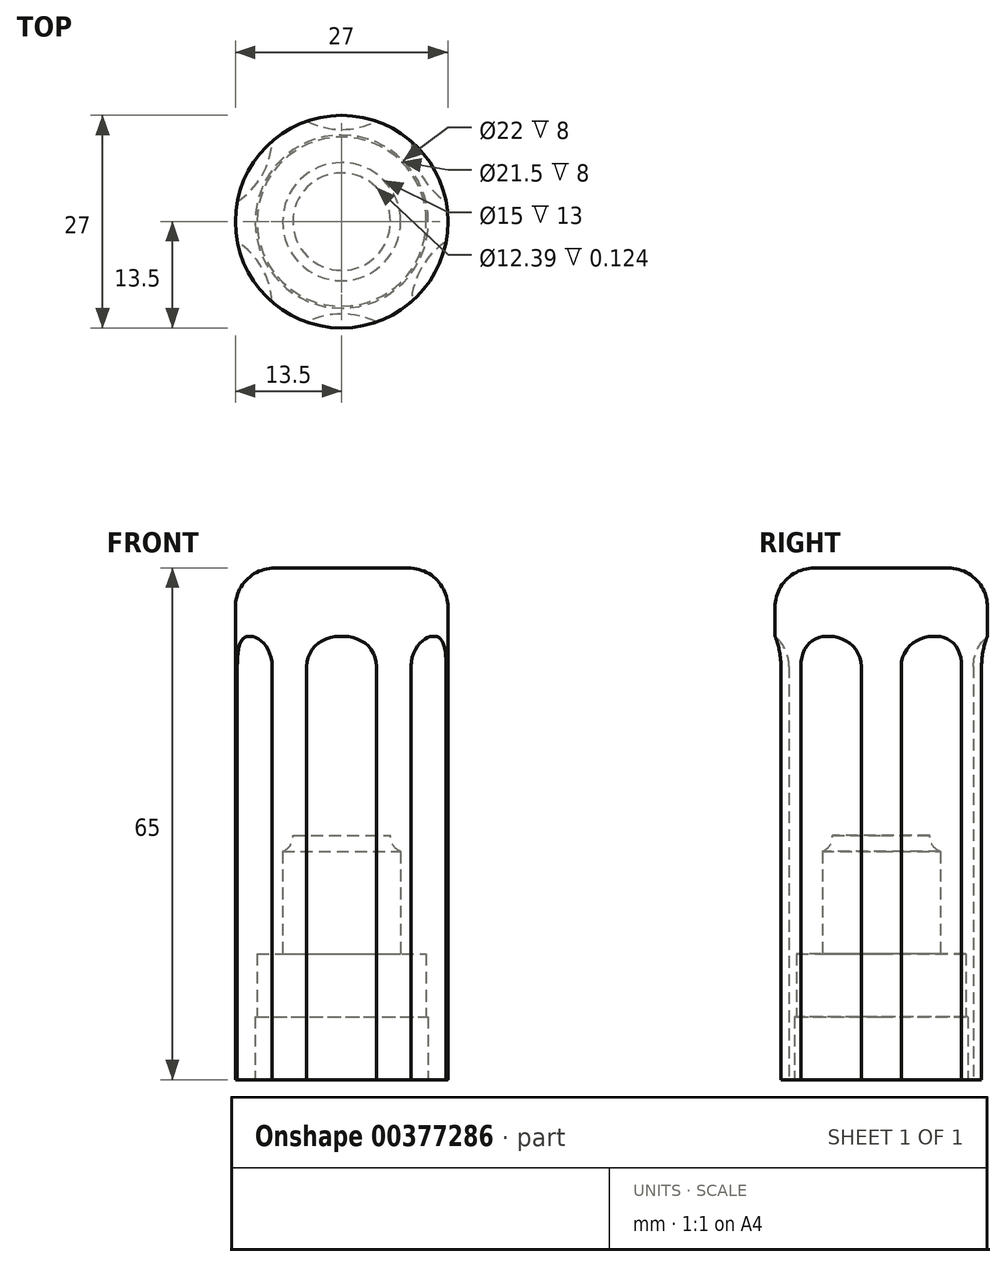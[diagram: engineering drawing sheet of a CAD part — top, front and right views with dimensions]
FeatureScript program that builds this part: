
annotation { "Feature Type Name" : "Feature", "Feature Type Description" : "" }
export const myFeature = defineFeature(function(context is Context, id is Id, definition is map)
    precondition{}
    {
        {
            var Q0;
            Q0=qCreatedBy(makeId("Front.planeOp"),FACE);
            var sketch = newSketch(context, id + "F0", { "sketchPlane" : qUnion([Q0])});
            skLineSegment(sketch, "E0", {"start": v(0, 32.45) * mm, "end": v(0, -32.55) * mm});
            skPoint(sketch, "E1.end.orphan", {"position": v(18.69, -28.88) * mm});
            skPoint(sketch, "E2.end.orphan", {"position": v(18.69, -32.55) * mm});
            skLineSegment(sketch, "E3", {"start": v(0, -32.55) * mm, "end": v(13.5, -32.55) * mm});
            skLineSegment(sketch, "E4", {"start": v(13.5, -32.55) * mm, "end": v(13.5, 27.45) * mm});
            skLineSegment(sketch, "E5", {"start": v(8.5, 32.45) * mm, "end": v(0, 32.45) * mm});
            skPoint(sketch, "E6.visualSharp", {"position": v(13.5, 32.45) * mm});
            skArc(sketch, "E6.filletArc", {"start": v(13.5, 27.45) * mm, "mid": v(12.04, 30.99) * mm, "end": v(8.5, 32.45) * mm});
            skSolve(sketch);
        }
        {
            var Q0;
            Q0=qSketchRegion(id+"F0",true);
            var Q1;
            Q1=sQuery(id+"F0.wireOp",EDGE,"E0");
            revolve(context, id + "F1", {"entities" : qUnion([Q0]), "axis" : qUnion([Q1]), "revolveType" : RevolveType.FULL});
        }
        {
            var Q0;
            Q0=makeQuery(id+"F1.opRevolve","SWEPT_FACE",FACE,{"disambiguationData":[OSD([sQuery(id+"F0.wireOp",EDGE,"E3")])]});
            var sketch = newSketch(context, id + "F2", { "sketchPlane" : qUnion([Q0])});
            skCircle(sketch, "E7.cCircle", {"center": v(0, 0) * mm, "radius": 13.5 * mm, "construction": true});
            skLineSegment(sketch, "E7.0", {"start": v(-13.5, -7.8) * mm, "end": v(-13.5, 7.8) * mm});
            skLineSegment(sketch, "E7.1", {"start": v(-13.5, 7.8) * mm, "end": v(0, 15.59) * mm});
            skLineSegment(sketch, "E7.2", {"start": v(0, 15.59) * mm, "end": v(13.5, 7.8) * mm});
            skLineSegment(sketch, "E7.3", {"start": v(13.5, 7.8) * mm, "end": v(13.5, -7.8) * mm});
            skLineSegment(sketch, "E7.4", {"start": v(13.5, -7.8) * mm, "end": v(0, -15.59) * mm});
            skLineSegment(sketch, "E7.5", {"start": v(0, -15.59) * mm, "end": v(-13.5, -7.8) * mm});
            skPoint(sketch, "E7.0.midPoint", {"position": v(-13.5, 0) * mm});
            skLineSegment(sketch, "E8.0", {"start": v(-13.5, -4.91) * mm, "end": v(-13.5, 4.91) * mm});
            skLineSegment(sketch, "E8.1", {"start": v(-13.5, 4.91) * mm, "end": v(-7.18, 12.44) * mm});
            skLineSegment(sketch, "E8.2", {"start": v(-7.18, 12.44) * mm, "end": v(2.5, 14.15) * mm});
            skLineSegment(sketch, "E8.3", {"start": v(2.5, 14.15) * mm, "end": v(11, 9.23) * mm});
            skLineSegment(sketch, "E8.4", {"start": v(11, 9.23) * mm, "end": v(14.37, 0) * mm});
            skLineSegment(sketch, "E8.5", {"start": v(14.37, 0) * mm, "end": v(11, -9.23) * mm});
            skLineSegment(sketch, "E8.6", {"start": v(11, -9.23) * mm, "end": v(2.5, -14.15) * mm});
            skLineSegment(sketch, "E8.7", {"start": v(2.5, -14.15) * mm, "end": v(-7.18, -12.44) * mm});
            skLineSegment(sketch, "E8.8", {"start": v(-7.18, -12.44) * mm, "end": v(-13.5, -4.91) * mm});
            skLineSegment(sketch, "E9.0", {"start": v(13.5, 4.91) * mm, "end": v(13.5, -4.91) * mm});
            skLineSegment(sketch, "E9.1", {"start": v(13.5, -4.91) * mm, "end": v(7.18, -12.44) * mm});
            skLineSegment(sketch, "E9.2", {"start": v(7.18, -12.44) * mm, "end": v(-2.5, -14.15) * mm});
            skLineSegment(sketch, "E9.3", {"start": v(-2.5, -14.15) * mm, "end": v(-11, -9.23) * mm});
            skLineSegment(sketch, "E9.4", {"start": v(-11, -9.23) * mm, "end": v(-14.37, 0) * mm});
            skLineSegment(sketch, "E9.5", {"start": v(-14.37, 0) * mm, "end": v(-11, 9.23) * mm});
            skLineSegment(sketch, "E9.6", {"start": v(-11, 9.23) * mm, "end": v(-2.5, 14.15) * mm});
            skLineSegment(sketch, "E9.7", {"start": v(-2.5, 14.15) * mm, "end": v(7.18, 12.44) * mm});
            skLineSegment(sketch, "E9.8", {"start": v(7.18, 12.44) * mm, "end": v(13.5, 4.91) * mm});
            skPoint(sketch, "E9.0.midPoint", {"position": v(13.5, 0) * mm});
            skArc(sketch, "E10", {"start": v(-4.69, 12.88) * mm, "mid": v(0, 11.71) * mm, "end": v(4.69, 12.88) * mm});
            skArc(sketch, "E11", {"start": v(4.69, -12.88) * mm, "mid": v(0, -11.71) * mm, "end": v(-4.69, -12.88) * mm});
            skArc(sketch, "E12", {"start": v(-13.5, 2.38) * mm, "mid": v(-10.14, 5.86) * mm, "end": v(-8.81, 10.5) * mm});
            skArc(sketch, "E13", {"start": v(-8.81, -10.5) * mm, "mid": v(-10.14, -5.86) * mm, "end": v(-13.5, -2.38) * mm});
            skArc(sketch, "E14", {"start": v(13.5, -2.38) * mm, "mid": v(10.14, -5.86) * mm, "end": v(8.81, -10.5) * mm});
            skArc(sketch, "E15", {"start": v(8.81, 10.5) * mm, "mid": v(10.14, 5.86) * mm, "end": v(13.5, 2.38) * mm});
            skCircle(sketch, "E16", {"center": v(0, 0) * mm, "radius": 11.23 * mm});
            skSolve(sketch);
        }
        {
            var Q0;
            {var subQ0=sQuery(id+"F2.wireOp",EDGE,"E7.5");var subQ1=sQuery(id+"F2.wireOp",EDGE,"E7.0");var subQ2=makeQuery(id+"F2.imprint","INTERSECT",VERTEX,{"derivedFrom":[subQ1,subQ0]});Q0=makeQuery(id+"F2.imprint","IMPRINT",FACE,{"disambiguationData":[TD([[makeQuery(id+"F2.imprint","IMPRINT",EDGE,{"disambiguationData":[TD([[subQ2,-1.0]])],"derivedFrom":subQ1}),-1.0]])]});}
            var Q1;
            {var subQ0=sQuery(id+"F2.wireOp",EDGE,"E7.1");var subQ1=sQuery(id+"F2.wireOp",EDGE,"E7.0");var subQ2=makeQuery(id+"F2.imprint","INTERSECT",VERTEX,{"derivedFrom":[subQ1,subQ0]});Q1=makeQuery(id+"F2.imprint","IMPRINT",FACE,{"disambiguationData":[TD([[makeQuery(id+"F2.imprint","IMPRINT",EDGE,{"disambiguationData":[TD([[subQ2,1.0]])],"derivedFrom":subQ1}),-1.0]])]});}
            var Q2;
            {var subQ0=sQuery(id+"F2.wireOp",EDGE,"E7.2");var subQ1=sQuery(id+"F2.wireOp",EDGE,"E7.1");var subQ2=makeQuery(id+"F2.imprint","INTERSECT",VERTEX,{"derivedFrom":[subQ1,subQ0]});Q2=makeQuery(id+"F2.imprint","IMPRINT",FACE,{"disambiguationData":[TD([[makeQuery(id+"F2.imprint","IMPRINT",EDGE,{"disambiguationData":[TD([[subQ2,1.0]])],"derivedFrom":subQ1}),-1.0]])]});}
            var Q3;
            {var subQ0=sQuery(id+"F2.wireOp",EDGE,"E7.3");var subQ1=sQuery(id+"F2.wireOp",EDGE,"E7.2");var subQ2=makeQuery(id+"F2.imprint","INTERSECT",VERTEX,{"derivedFrom":[subQ1,subQ0]});Q3=makeQuery(id+"F2.imprint","IMPRINT",FACE,{"disambiguationData":[TD([[makeQuery(id+"F2.imprint","IMPRINT",EDGE,{"disambiguationData":[TD([[subQ2,1.0]])],"derivedFrom":subQ1}),-1.0]])]});}
            var Q4;
            {var subQ0=sQuery(id+"F2.wireOp",EDGE,"E7.4");var subQ1=sQuery(id+"F2.wireOp",EDGE,"E7.3");var subQ2=makeQuery(id+"F2.imprint","INTERSECT",VERTEX,{"derivedFrom":[subQ1,subQ0]});Q4=makeQuery(id+"F2.imprint","IMPRINT",FACE,{"disambiguationData":[TD([[makeQuery(id+"F2.imprint","IMPRINT",EDGE,{"disambiguationData":[TD([[subQ2,1.0]])],"derivedFrom":subQ1}),-1.0]])]});}
            var Q5;
            {var subQ0=sQuery(id+"F2.wireOp",EDGE,"E7.5");var subQ1=sQuery(id+"F2.wireOp",EDGE,"E7.4");var subQ2=makeQuery(id+"F2.imprint","INTERSECT",VERTEX,{"derivedFrom":[subQ1,subQ0]});Q5=makeQuery(id+"F2.imprint","IMPRINT",FACE,{"disambiguationData":[TD([[makeQuery(id+"F2.imprint","IMPRINT",EDGE,{"disambiguationData":[TD([[subQ2,1.0]])],"derivedFrom":subQ1}),-1.0]])]});}
            var Q6;
            {var subQ0=sQuery(id+"F2.wireOp",EDGE,"E9.4");var subQ4=sQuery(id+"F2.wireOp",EDGE,"E9.5");var subQ5=makeQuery(id+"F2.imprint","INTERSECT",VERTEX,{"derivedFrom":[subQ0,subQ4]});Q6=makeQuery(id+"F2.imprint","IMPRINT",FACE,{"disambiguationData":[TD([[makeQuery(id+"F2.imprint","IMPRINT",EDGE,{"disambiguationData":[TD([[subQ5,1.0]])],"derivedFrom":subQ0}),-1.0]])]});}
            var Q7;
            {var subQ0=sQuery(id+"F2.wireOp",EDGE,"E8.2");var subQ1=sQuery(id+"F2.wireOp",EDGE,"E8.1");var subQ2=makeQuery(id+"F2.imprint","INTERSECT",VERTEX,{"derivedFrom":[subQ1,subQ0]});Q7=makeQuery(id+"F2.imprint","IMPRINT",FACE,{"disambiguationData":[TD([[makeQuery(id+"F2.imprint","IMPRINT",EDGE,{"disambiguationData":[TD([[subQ2,1.0]])],"derivedFrom":subQ1}),-1.0]])]});}
            var Q8;
            {var subQ0=sQuery(id+"F2.wireOp",EDGE,"E9.7");var subQ4=sQuery(id+"F2.wireOp",EDGE,"E9.8");var subQ5=makeQuery(id+"F2.imprint","INTERSECT",VERTEX,{"derivedFrom":[subQ0,subQ4]});Q8=makeQuery(id+"F2.imprint","IMPRINT",FACE,{"disambiguationData":[TD([[makeQuery(id+"F2.imprint","IMPRINT",EDGE,{"disambiguationData":[TD([[subQ5,1.0]])],"derivedFrom":subQ0}),-1.0]])]});}
            var Q9;
            {var subQ0=sQuery(id+"F2.wireOp",EDGE,"E8.5");var subQ1=sQuery(id+"F2.wireOp",EDGE,"E8.4");var subQ2=makeQuery(id+"F2.imprint","INTERSECT",VERTEX,{"derivedFrom":[subQ1,subQ0]});Q9=makeQuery(id+"F2.imprint","IMPRINT",FACE,{"disambiguationData":[TD([[makeQuery(id+"F2.imprint","IMPRINT",EDGE,{"disambiguationData":[TD([[subQ2,1.0]])],"derivedFrom":subQ1}),-1.0]])]});}
            var Q10;
            {var subQ0=sQuery(id+"F2.wireOp",EDGE,"E9.1");var subQ4=sQuery(id+"F2.wireOp",EDGE,"E9.2");var subQ6=makeQuery(id+"F2.imprint","INTERSECT",VERTEX,{"derivedFrom":[subQ0,subQ4]});Q10=makeQuery(id+"F2.imprint","IMPRINT",FACE,{"disambiguationData":[TD([[makeQuery(id+"F2.imprint","IMPRINT",EDGE,{"disambiguationData":[TD([[subQ6,1.0]])],"derivedFrom":subQ0}),-1.0]])]});}
            var Q11;
            {var subQ0=sQuery(id+"F2.wireOp",EDGE,"E8.8");var subQ1=sQuery(id+"F2.wireOp",EDGE,"E8.7");var subQ2=makeQuery(id+"F2.imprint","INTERSECT",VERTEX,{"derivedFrom":[subQ1,subQ0]});Q11=makeQuery(id+"F2.imprint","IMPRINT",FACE,{"disambiguationData":[TD([[makeQuery(id+"F2.imprint","IMPRINT",EDGE,{"disambiguationData":[TD([[subQ2,1.0]])],"derivedFrom":subQ1}),-1.0]])]});}
            var Q12;
            {var subQ0=sQuery(id+"F2.wireOp",EDGE,"E8.8");var subQ3=sQuery(id+"F2.wireOp",EDGE,"E9.4");var subQ5=makeQuery(id+"F2.imprint","INTERSECT",VERTEX,{"derivedFrom":[subQ0,subQ3]});Q12=makeQuery(id+"F2.imprint","IMPRINT",FACE,{"disambiguationData":[TD([[makeQuery(id+"F2.imprint","IMPRINT",EDGE,{"disambiguationData":[TD([[subQ5,-1.0]])],"derivedFrom":subQ0}),-1.0]])]});}
            var Q13;
            {var subQ0=sQuery(id+"F2.wireOp",EDGE,"E8.1");var subQ3=sQuery(id+"F2.wireOp",EDGE,"E9.5");var subQ5=makeQuery(id+"F2.imprint","INTERSECT",VERTEX,{"derivedFrom":[subQ0,subQ3]});Q13=makeQuery(id+"F2.imprint","IMPRINT",FACE,{"disambiguationData":[TD([[makeQuery(id+"F2.imprint","IMPRINT",EDGE,{"disambiguationData":[TD([[subQ5,1.0]])],"derivedFrom":subQ0}),-1.0]])]});}
            var Q14;
            {var subQ0=sQuery(id+"F2.wireOp",EDGE,"E9.5");var subQ1=sQuery(id+"F2.wireOp",EDGE,"E8.1");var subQ2=makeQuery(id+"F2.imprint","INTERSECT",VERTEX,{"derivedFrom":[subQ1,subQ0]});Q14=makeQuery(id+"F2.imprint","IMPRINT",FACE,{"disambiguationData":[TD([[makeQuery(id+"F2.imprint","IMPRINT",EDGE,{"disambiguationData":[TD([[subQ2,-1.0]])],"derivedFrom":subQ1}),1.0]])]});}
            var Q15;
            {var subQ1=sQuery(id+"F2.wireOp",EDGE,"E8.2");var subQ4=sQuery(id+"F2.wireOp",EDGE,"E9.7");var subQ6=makeQuery(id+"F2.imprint","INTERSECT",VERTEX,{"derivedFrom":[subQ1,subQ4]});Q15=makeQuery(id+"F2.imprint","IMPRINT",FACE,{"disambiguationData":[TD([[makeQuery(id+"F2.imprint","IMPRINT",EDGE,{"disambiguationData":[TD([[subQ6,1.0]])],"derivedFrom":subQ1}),1.0]])]});}
            var Q16;
            {var subQ1=sQuery(id+"F2.wireOp",EDGE,"E8.2");var subQ3=sQuery(id+"F2.wireOp",EDGE,"E9.7");var subQ4=makeQuery(id+"F2.imprint","INTERSECT",VERTEX,{"derivedFrom":[subQ1,subQ3]});Q16=makeQuery(id+"F2.imprint","IMPRINT",FACE,{"disambiguationData":[TD([[makeQuery(id+"F2.imprint","IMPRINT",EDGE,{"disambiguationData":[TD([[subQ4,-1.0]])],"derivedFrom":subQ1}),-1.0]])]});}
            var Q17;
            {var subQ0=sQuery(id+"F2.wireOp",EDGE,"E8.4");var subQ3=sQuery(id+"F2.wireOp",EDGE,"E9.8");var subQ5=makeQuery(id+"F2.imprint","INTERSECT",VERTEX,{"derivedFrom":[subQ0,subQ3]});Q17=makeQuery(id+"F2.imprint","IMPRINT",FACE,{"disambiguationData":[TD([[makeQuery(id+"F2.imprint","IMPRINT",EDGE,{"disambiguationData":[TD([[subQ5,1.0]])],"derivedFrom":subQ0}),-1.0]])]});}
            var Q18;
            {var subQ0=sQuery(id+"F2.wireOp",EDGE,"E9.8");var subQ1=sQuery(id+"F2.wireOp",EDGE,"E8.4");var subQ2=makeQuery(id+"F2.imprint","INTERSECT",VERTEX,{"derivedFrom":[subQ1,subQ0]});Q18=makeQuery(id+"F2.imprint","IMPRINT",FACE,{"disambiguationData":[TD([[makeQuery(id+"F2.imprint","IMPRINT",EDGE,{"disambiguationData":[TD([[subQ2,-1.0]])],"derivedFrom":subQ1}),1.0]])]});}
            var Q19;
            {var subQ1=sQuery(id+"F2.wireOp",EDGE,"E8.5");var subQ4=sQuery(id+"F2.wireOp",EDGE,"E9.1");var subQ5=makeQuery(id+"F2.imprint","INTERSECT",VERTEX,{"derivedFrom":[subQ1,subQ4]});Q19=makeQuery(id+"F2.imprint","IMPRINT",FACE,{"disambiguationData":[TD([[makeQuery(id+"F2.imprint","IMPRINT",EDGE,{"disambiguationData":[TD([[subQ5,1.0]])],"derivedFrom":subQ1}),1.0]])]});}
            var Q20;
            {var subQ1=sQuery(id+"F2.wireOp",EDGE,"E8.5");var subQ3=sQuery(id+"F2.wireOp",EDGE,"E9.1");var subQ4=makeQuery(id+"F2.imprint","INTERSECT",VERTEX,{"derivedFrom":[subQ1,subQ3]});Q20=makeQuery(id+"F2.imprint","IMPRINT",FACE,{"disambiguationData":[TD([[makeQuery(id+"F2.imprint","IMPRINT",EDGE,{"disambiguationData":[TD([[subQ4,-1.0]])],"derivedFrom":subQ1}),-1.0]])]});}
            var Q21;
            {var subQ0=sQuery(id+"F2.wireOp",EDGE,"E8.7");var subQ3=sQuery(id+"F2.wireOp",EDGE,"E9.2");var subQ5=makeQuery(id+"F2.imprint","INTERSECT",VERTEX,{"derivedFrom":[subQ0,subQ3]});Q21=makeQuery(id+"F2.imprint","IMPRINT",FACE,{"disambiguationData":[TD([[makeQuery(id+"F2.imprint","IMPRINT",EDGE,{"disambiguationData":[TD([[subQ5,1.0]])],"derivedFrom":subQ0}),-1.0]])]});}
            var Q22;
            {var subQ0=sQuery(id+"F2.wireOp",EDGE,"E9.2");var subQ1=sQuery(id+"F2.wireOp",EDGE,"E8.7");var subQ2=makeQuery(id+"F2.imprint","INTERSECT",VERTEX,{"derivedFrom":[subQ1,subQ0]});Q22=makeQuery(id+"F2.imprint","IMPRINT",FACE,{"disambiguationData":[TD([[makeQuery(id+"F2.imprint","IMPRINT",EDGE,{"disambiguationData":[TD([[subQ2,-1.0]])],"derivedFrom":subQ1}),1.0]])]});}
            var Q23;
            {var subQ1=sQuery(id+"F2.wireOp",EDGE,"E8.8");var subQ4=sQuery(id+"F2.wireOp",EDGE,"E9.4");var subQ5=makeQuery(id+"F2.imprint","INTERSECT",VERTEX,{"derivedFrom":[subQ1,subQ4]});Q23=makeQuery(id+"F2.imprint","IMPRINT",FACE,{"disambiguationData":[TD([[makeQuery(id+"F2.imprint","IMPRINT",EDGE,{"disambiguationData":[TD([[subQ5,1.0]])],"derivedFrom":subQ1}),1.0]])]});}
            var Q24;
            {var subQ0=sQuery(id+"F2.wireOp",EDGE,"E13");var subQ1=sQuery(id+"F2.wireOp",EDGE,"E8.0");var subQ2=makeQuery(id+"F2.imprint","INTERSECT",VERTEX,{"derivedFrom":[subQ1,sQuery(id+"F2.wireOp",EDGE,"E9.4"),subQ0]});Q24=makeQuery(id+"F2.imprint","IMPRINT",FACE,{"disambiguationData":[TD([[makeQuery(id+"F2.imprint","IMPRINT",EDGE,{"disambiguationData":[TD([[subQ2,-1.0]])],"derivedFrom":subQ1}),-1.0]])]});}
            var Q25;
            {var subQ0=sQuery(id+"F2.wireOp",EDGE,"E12");var subQ1=sQuery(id+"F2.wireOp",EDGE,"E8.0");var subQ2=makeQuery(id+"F2.imprint","INTERSECT",VERTEX,{"derivedFrom":[subQ1,sQuery(id+"F2.wireOp",EDGE,"E9.5"),subQ0]});Q25=makeQuery(id+"F2.imprint","IMPRINT",FACE,{"disambiguationData":[TD([[makeQuery(id+"F2.imprint","IMPRINT",EDGE,{"disambiguationData":[TD([[subQ2,1.0]])],"derivedFrom":subQ1}),-1.0]])]});}
            var Q26;
            {var subQ0=sQuery(id+"F2.wireOp",EDGE,"E9.5");var subQ1=sQuery(id+"F2.wireOp",EDGE,"E8.1");var subQ2=makeQuery(id+"F2.imprint","INTERSECT",VERTEX,{"derivedFrom":[subQ1,subQ0]});Q26=makeQuery(id+"F2.imprint","IMPRINT",FACE,{"disambiguationData":[TD([[makeQuery(id+"F2.imprint","IMPRINT",EDGE,{"disambiguationData":[TD([[subQ2,-1.0]])],"derivedFrom":subQ1}),-1.0]])]});}
            var Q27;
            {var subQ0=sQuery(id+"F2.wireOp",EDGE,"E12");var subQ1=sQuery(id+"F2.wireOp",EDGE,"E8.1");var subQ2=makeQuery(id+"F2.imprint","INTERSECT",VERTEX,{"derivedFrom":[subQ1,sQuery(id+"F2.wireOp",EDGE,"E9.6"),subQ0]});Q27=makeQuery(id+"F2.imprint","IMPRINT",FACE,{"disambiguationData":[TD([[makeQuery(id+"F2.imprint","IMPRINT",EDGE,{"disambiguationData":[TD([[subQ2,1.0]])],"derivedFrom":subQ1}),-1.0]])]});}
            var Q28;
            {var subQ0=sQuery(id+"F2.wireOp",EDGE,"E10");var subQ1=sQuery(id+"F2.wireOp",EDGE,"E8.2");var subQ2=makeQuery(id+"F2.imprint","INTERSECT",VERTEX,{"derivedFrom":[subQ1,sQuery(id+"F2.wireOp",EDGE,"E9.6"),subQ0]});Q28=makeQuery(id+"F2.imprint","IMPRINT",FACE,{"disambiguationData":[TD([[makeQuery(id+"F2.imprint","IMPRINT",EDGE,{"disambiguationData":[TD([[subQ2,-1.0]])],"derivedFrom":subQ1}),-1.0]])]});}
            var Q29;
            {var subQ0=sQuery(id+"F2.wireOp",EDGE,"E9.7");var subQ1=sQuery(id+"F2.wireOp",EDGE,"E8.2");var subQ2=makeQuery(id+"F2.imprint","INTERSECT",VERTEX,{"derivedFrom":[subQ1,subQ0]});Q29=makeQuery(id+"F2.imprint","IMPRINT",FACE,{"disambiguationData":[TD([[makeQuery(id+"F2.imprint","IMPRINT",EDGE,{"disambiguationData":[TD([[subQ2,1.0]])],"derivedFrom":subQ1}),-1.0]])]});}
            var Q30;
            {var subQ0=sQuery(id+"F2.wireOp",EDGE,"E10");var subQ1=sQuery(id+"F2.wireOp",EDGE,"E8.3");var subQ2=makeQuery(id+"F2.imprint","INTERSECT",VERTEX,{"derivedFrom":[subQ1,sQuery(id+"F2.wireOp",EDGE,"E9.7"),subQ0]});Q30=makeQuery(id+"F2.imprint","IMPRINT",FACE,{"disambiguationData":[TD([[makeQuery(id+"F2.imprint","IMPRINT",EDGE,{"disambiguationData":[TD([[subQ2,-1.0]])],"derivedFrom":subQ1}),-1.0]])]});}
            var Q31;
            {var subQ0=sQuery(id+"F2.wireOp",EDGE,"E15");var subQ1=sQuery(id+"F2.wireOp",EDGE,"E8.3");var subQ2=makeQuery(id+"F2.imprint","INTERSECT",VERTEX,{"derivedFrom":[subQ1,sQuery(id+"F2.wireOp",EDGE,"E9.8"),subQ0]});Q31=makeQuery(id+"F2.imprint","IMPRINT",FACE,{"disambiguationData":[TD([[makeQuery(id+"F2.imprint","IMPRINT",EDGE,{"disambiguationData":[TD([[subQ2,1.0]])],"derivedFrom":subQ1}),-1.0]])]});}
            var Q32;
            {var subQ0=sQuery(id+"F2.wireOp",EDGE,"E9.8");var subQ1=sQuery(id+"F2.wireOp",EDGE,"E8.4");var subQ2=makeQuery(id+"F2.imprint","INTERSECT",VERTEX,{"derivedFrom":[subQ1,subQ0]});Q32=makeQuery(id+"F2.imprint","IMPRINT",FACE,{"disambiguationData":[TD([[makeQuery(id+"F2.imprint","IMPRINT",EDGE,{"disambiguationData":[TD([[subQ2,-1.0]])],"derivedFrom":subQ1}),-1.0]])]});}
            var Q33;
            {var subQ0=sQuery(id+"F2.wireOp",EDGE,"E15");var subQ1=sQuery(id+"F2.wireOp",EDGE,"E8.4");var subQ2=makeQuery(id+"F2.imprint","INTERSECT",VERTEX,{"derivedFrom":[subQ1,sQuery(id+"F2.wireOp",EDGE,"E9.0"),subQ0]});Q33=makeQuery(id+"F2.imprint","IMPRINT",FACE,{"disambiguationData":[TD([[makeQuery(id+"F2.imprint","IMPRINT",EDGE,{"disambiguationData":[TD([[subQ2,1.0]])],"derivedFrom":subQ1}),-1.0]])]});}
            var Q34;
            {var subQ0=sQuery(id+"F2.wireOp",EDGE,"E14");var subQ1=sQuery(id+"F2.wireOp",EDGE,"E8.5");var subQ2=makeQuery(id+"F2.imprint","INTERSECT",VERTEX,{"derivedFrom":[subQ1,sQuery(id+"F2.wireOp",EDGE,"E9.0"),subQ0]});Q34=makeQuery(id+"F2.imprint","IMPRINT",FACE,{"disambiguationData":[TD([[makeQuery(id+"F2.imprint","IMPRINT",EDGE,{"disambiguationData":[TD([[subQ2,-1.0]])],"derivedFrom":subQ1}),-1.0]])]});}
            var Q35;
            {var subQ0=sQuery(id+"F2.wireOp",EDGE,"E9.1");var subQ1=sQuery(id+"F2.wireOp",EDGE,"E8.5");var subQ2=makeQuery(id+"F2.imprint","INTERSECT",VERTEX,{"derivedFrom":[subQ1,subQ0]});Q35=makeQuery(id+"F2.imprint","IMPRINT",FACE,{"disambiguationData":[TD([[makeQuery(id+"F2.imprint","IMPRINT",EDGE,{"disambiguationData":[TD([[subQ2,1.0]])],"derivedFrom":subQ1}),-1.0]])]});}
            var Q36;
            {var subQ0=sQuery(id+"F2.wireOp",EDGE,"E14");var subQ1=sQuery(id+"F2.wireOp",EDGE,"E8.6");var subQ2=makeQuery(id+"F2.imprint","INTERSECT",VERTEX,{"derivedFrom":[subQ1,sQuery(id+"F2.wireOp",EDGE,"E9.1"),subQ0]});Q36=makeQuery(id+"F2.imprint","IMPRINT",FACE,{"disambiguationData":[TD([[makeQuery(id+"F2.imprint","IMPRINT",EDGE,{"disambiguationData":[TD([[subQ2,-1.0]])],"derivedFrom":subQ1}),-1.0]])]});}
            var Q37;
            {var subQ0=sQuery(id+"F2.wireOp",EDGE,"E11");var subQ1=sQuery(id+"F2.wireOp",EDGE,"E8.6");var subQ2=makeQuery(id+"F2.imprint","INTERSECT",VERTEX,{"derivedFrom":[subQ1,sQuery(id+"F2.wireOp",EDGE,"E9.2"),subQ0]});Q37=makeQuery(id+"F2.imprint","IMPRINT",FACE,{"disambiguationData":[TD([[makeQuery(id+"F2.imprint","IMPRINT",EDGE,{"disambiguationData":[TD([[subQ2,1.0]])],"derivedFrom":subQ1}),-1.0]])]});}
            var Q38;
            {var subQ0=sQuery(id+"F2.wireOp",EDGE,"E9.2");var subQ1=sQuery(id+"F2.wireOp",EDGE,"E8.7");var subQ2=makeQuery(id+"F2.imprint","INTERSECT",VERTEX,{"derivedFrom":[subQ1,subQ0]});Q38=makeQuery(id+"F2.imprint","IMPRINT",FACE,{"disambiguationData":[TD([[makeQuery(id+"F2.imprint","IMPRINT",EDGE,{"disambiguationData":[TD([[subQ2,-1.0]])],"derivedFrom":subQ1}),-1.0]])]});}
            var Q39;
            {var subQ0=sQuery(id+"F2.wireOp",EDGE,"E11");var subQ1=sQuery(id+"F2.wireOp",EDGE,"E8.7");var subQ2=makeQuery(id+"F2.imprint","INTERSECT",VERTEX,{"derivedFrom":[subQ1,sQuery(id+"F2.wireOp",EDGE,"E9.3"),subQ0]});Q39=makeQuery(id+"F2.imprint","IMPRINT",FACE,{"disambiguationData":[TD([[makeQuery(id+"F2.imprint","IMPRINT",EDGE,{"disambiguationData":[TD([[subQ2,1.0]])],"derivedFrom":subQ1}),-1.0]])]});}
            var Q40;
            {var subQ0=sQuery(id+"F2.wireOp",EDGE,"E13");var subQ1=sQuery(id+"F2.wireOp",EDGE,"E8.8");var subQ2=makeQuery(id+"F2.imprint","INTERSECT",VERTEX,{"derivedFrom":[subQ1,sQuery(id+"F2.wireOp",EDGE,"E9.3"),subQ0]});Q40=makeQuery(id+"F2.imprint","IMPRINT",FACE,{"disambiguationData":[TD([[makeQuery(id+"F2.imprint","IMPRINT",EDGE,{"disambiguationData":[TD([[subQ2,-1.0]])],"derivedFrom":subQ1}),-1.0]])]});}
            var Q41;
            {var subQ0=sQuery(id+"F2.wireOp",EDGE,"E9.4");var subQ1=sQuery(id+"F2.wireOp",EDGE,"E8.8");var subQ2=makeQuery(id+"F2.imprint","INTERSECT",VERTEX,{"derivedFrom":[subQ1,subQ0]});Q41=makeQuery(id+"F2.imprint","IMPRINT",FACE,{"disambiguationData":[TD([[makeQuery(id+"F2.imprint","IMPRINT",EDGE,{"disambiguationData":[TD([[subQ2,1.0]])],"derivedFrom":subQ1}),-1.0]])]});}
            var Q42;
            {var subQ0=sQuery(id+"F2.wireOp",EDGE,"E15");var subQ1=sQuery(id+"F2.wireOp",EDGE,"E9.0");var subQ2=makeQuery(id+"F2.imprint","INTERSECT",VERTEX,{"derivedFrom":[sQuery(id+"F2.wireOp",EDGE,"E8.4"),subQ1,subQ0]});Q42=makeQuery(id+"F2.imprint","IMPRINT",FACE,{"disambiguationData":[TD([[makeQuery(id+"F2.imprint","IMPRINT",EDGE,{"disambiguationData":[TD([[subQ2,-1.0]])],"derivedFrom":subQ1}),-1.0]])]});}
            var Q43;
            {var subQ0=sQuery(id+"F2.wireOp",EDGE,"E14");var subQ1=sQuery(id+"F2.wireOp",EDGE,"E9.0");var subQ2=makeQuery(id+"F2.imprint","INTERSECT",VERTEX,{"derivedFrom":[sQuery(id+"F2.wireOp",EDGE,"E8.5"),subQ1,subQ0]});Q43=makeQuery(id+"F2.imprint","IMPRINT",FACE,{"disambiguationData":[TD([[makeQuery(id+"F2.imprint","IMPRINT",EDGE,{"disambiguationData":[TD([[subQ2,1.0]])],"derivedFrom":subQ1}),-1.0]])]});}
            var Q44;
            {var subQ0=sQuery(id+"F2.wireOp",EDGE,"E14");var subQ1=sQuery(id+"F2.wireOp",EDGE,"E9.1");var subQ2=makeQuery(id+"F2.imprint","INTERSECT",VERTEX,{"derivedFrom":[sQuery(id+"F2.wireOp",EDGE,"E8.6"),subQ1,subQ0]});Q44=makeQuery(id+"F2.imprint","IMPRINT",FACE,{"disambiguationData":[TD([[makeQuery(id+"F2.imprint","IMPRINT",EDGE,{"disambiguationData":[TD([[subQ2,1.0]])],"derivedFrom":subQ1}),-1.0]])]});}
            var Q45;
            {var subQ0=sQuery(id+"F2.wireOp",EDGE,"E11");var subQ1=sQuery(id+"F2.wireOp",EDGE,"E9.2");var subQ2=makeQuery(id+"F2.imprint","INTERSECT",VERTEX,{"derivedFrom":[sQuery(id+"F2.wireOp",EDGE,"E8.6"),subQ1,subQ0]});Q45=makeQuery(id+"F2.imprint","IMPRINT",FACE,{"disambiguationData":[TD([[makeQuery(id+"F2.imprint","IMPRINT",EDGE,{"disambiguationData":[TD([[subQ2,-1.0]])],"derivedFrom":subQ1}),-1.0]])]});}
            var Q46;
            {var subQ0=sQuery(id+"F2.wireOp",EDGE,"E11");var subQ1=sQuery(id+"F2.wireOp",EDGE,"E9.3");var subQ2=makeQuery(id+"F2.imprint","INTERSECT",VERTEX,{"derivedFrom":[sQuery(id+"F2.wireOp",EDGE,"E8.7"),subQ1,subQ0]});Q46=makeQuery(id+"F2.imprint","IMPRINT",FACE,{"disambiguationData":[TD([[makeQuery(id+"F2.imprint","IMPRINT",EDGE,{"disambiguationData":[TD([[subQ2,-1.0]])],"derivedFrom":subQ1}),-1.0]])]});}
            var Q47;
            {var subQ0=sQuery(id+"F2.wireOp",EDGE,"E13");var subQ1=sQuery(id+"F2.wireOp",EDGE,"E9.3");var subQ2=makeQuery(id+"F2.imprint","INTERSECT",VERTEX,{"derivedFrom":[sQuery(id+"F2.wireOp",EDGE,"E8.8"),subQ1,subQ0]});Q47=makeQuery(id+"F2.imprint","IMPRINT",FACE,{"disambiguationData":[TD([[makeQuery(id+"F2.imprint","IMPRINT",EDGE,{"disambiguationData":[TD([[subQ2,1.0]])],"derivedFrom":subQ1}),-1.0]])]});}
            var Q48;
            {var subQ0=sQuery(id+"F2.wireOp",EDGE,"E13");var subQ1=sQuery(id+"F2.wireOp",EDGE,"E9.4");var subQ2=makeQuery(id+"F2.imprint","INTERSECT",VERTEX,{"derivedFrom":[sQuery(id+"F2.wireOp",EDGE,"E8.0"),subQ1,subQ0]});Q48=makeQuery(id+"F2.imprint","IMPRINT",FACE,{"disambiguationData":[TD([[makeQuery(id+"F2.imprint","IMPRINT",EDGE,{"disambiguationData":[TD([[subQ2,1.0]])],"derivedFrom":subQ1}),-1.0]])]});}
            var Q49;
            {var subQ0=sQuery(id+"F2.wireOp",EDGE,"E12");var subQ1=sQuery(id+"F2.wireOp",EDGE,"E9.5");var subQ2=makeQuery(id+"F2.imprint","INTERSECT",VERTEX,{"derivedFrom":[sQuery(id+"F2.wireOp",EDGE,"E8.0"),subQ1,subQ0]});Q49=makeQuery(id+"F2.imprint","IMPRINT",FACE,{"disambiguationData":[TD([[makeQuery(id+"F2.imprint","IMPRINT",EDGE,{"disambiguationData":[TD([[subQ2,-1.0]])],"derivedFrom":subQ1}),-1.0]])]});}
            var Q50;
            {var subQ0=sQuery(id+"F2.wireOp",EDGE,"E12");var subQ1=sQuery(id+"F2.wireOp",EDGE,"E9.6");var subQ2=makeQuery(id+"F2.imprint","INTERSECT",VERTEX,{"derivedFrom":[sQuery(id+"F2.wireOp",EDGE,"E8.1"),subQ1,subQ0]});Q50=makeQuery(id+"F2.imprint","IMPRINT",FACE,{"disambiguationData":[TD([[makeQuery(id+"F2.imprint","IMPRINT",EDGE,{"disambiguationData":[TD([[subQ2,-1.0]])],"derivedFrom":subQ1}),-1.0]])]});}
            var Q51;
            {var subQ0=sQuery(id+"F2.wireOp",EDGE,"E10");var subQ1=sQuery(id+"F2.wireOp",EDGE,"E9.6");var subQ2=makeQuery(id+"F2.imprint","INTERSECT",VERTEX,{"derivedFrom":[sQuery(id+"F2.wireOp",EDGE,"E8.2"),subQ1,subQ0]});Q51=makeQuery(id+"F2.imprint","IMPRINT",FACE,{"disambiguationData":[TD([[makeQuery(id+"F2.imprint","IMPRINT",EDGE,{"disambiguationData":[TD([[subQ2,1.0]])],"derivedFrom":subQ1}),-1.0]])]});}
            var Q52;
            {var subQ0=sQuery(id+"F2.wireOp",EDGE,"E10");var subQ1=sQuery(id+"F2.wireOp",EDGE,"E9.7");var subQ2=makeQuery(id+"F2.imprint","INTERSECT",VERTEX,{"derivedFrom":[sQuery(id+"F2.wireOp",EDGE,"E8.3"),subQ1,subQ0]});Q52=makeQuery(id+"F2.imprint","IMPRINT",FACE,{"disambiguationData":[TD([[makeQuery(id+"F2.imprint","IMPRINT",EDGE,{"disambiguationData":[TD([[subQ2,1.0]])],"derivedFrom":subQ1}),-1.0]])]});}
            var Q53;
            {var subQ0=sQuery(id+"F2.wireOp",EDGE,"E15");var subQ1=sQuery(id+"F2.wireOp",EDGE,"E9.8");var subQ2=makeQuery(id+"F2.imprint","INTERSECT",VERTEX,{"derivedFrom":[sQuery(id+"F2.wireOp",EDGE,"E8.3"),subQ1,subQ0]});Q53=makeQuery(id+"F2.imprint","IMPRINT",FACE,{"disambiguationData":[TD([[makeQuery(id+"F2.imprint","IMPRINT",EDGE,{"disambiguationData":[TD([[subQ2,-1.0]])],"derivedFrom":subQ1}),-1.0]])]});}
            var Q54;
            {var subQ0=sQuery(id+"F2.wireOp",EDGE,"E10");var subQ1=makeQuery(id+"F1.opRevolve","SWEPT_EDGE",EDGE,{"disambiguationData":[OSD([sQuery(id+"F0.wireOp",EDGE,"E3"),sQuery(id+"F0.wireOp",EDGE,"E4")])]});var subQ2=makeQuery(id+"F2.imprint","INTERSECT",VERTEX,{"disambiguationData":[OD(0.0)],"derivedFrom":[subQ1,subQ0]});Q54=makeQuery(id+"F2.imprint","IMPRINT",FACE,{"disambiguationData":[TD([[makeQuery(id+"F2.imprint","IMPRINT",EDGE,{"disambiguationData":[TD([[subQ2,-1.0]])],"derivedFrom":subQ0}),1.0]])]});}
            var Q55;
            {var subQ0=sQuery(id+"F2.wireOp",EDGE,"E11");var subQ1=makeQuery(id+"F1.opRevolve","SWEPT_EDGE",EDGE,{"disambiguationData":[OSD([sQuery(id+"F0.wireOp",EDGE,"E3"),sQuery(id+"F0.wireOp",EDGE,"E4")])]});var subQ2=makeQuery(id+"F2.imprint","INTERSECT",VERTEX,{"disambiguationData":[OD(0.0)],"derivedFrom":[subQ1,subQ0]});Q55=makeQuery(id+"F2.imprint","IMPRINT",FACE,{"disambiguationData":[TD([[makeQuery(id+"F2.imprint","IMPRINT",EDGE,{"disambiguationData":[TD([[subQ2,-1.0]])],"derivedFrom":subQ0}),1.0]])]});}
            var Q56;
            {var subQ0=sQuery(id+"F2.wireOp",EDGE,"E12");var subQ1=makeQuery(id+"F1.opRevolve","SWEPT_EDGE",EDGE,{"disambiguationData":[OSD([sQuery(id+"F0.wireOp",EDGE,"E3"),sQuery(id+"F0.wireOp",EDGE,"E4")])]});var subQ2=makeQuery(id+"F2.imprint","INTERSECT",VERTEX,{"disambiguationData":[OD(0.0)],"derivedFrom":[subQ1,subQ0]});Q56=makeQuery(id+"F2.imprint","IMPRINT",FACE,{"disambiguationData":[TD([[makeQuery(id+"F2.imprint","IMPRINT",EDGE,{"disambiguationData":[TD([[subQ2,-1.0]])],"derivedFrom":subQ0}),1.0]])]});}
            var Q57;
            {var subQ0=sQuery(id+"F2.wireOp",EDGE,"E13");var subQ1=makeQuery(id+"F1.opRevolve","SWEPT_EDGE",EDGE,{"disambiguationData":[OSD([sQuery(id+"F0.wireOp",EDGE,"E3"),sQuery(id+"F0.wireOp",EDGE,"E4")])]});var subQ2=makeQuery(id+"F2.imprint","INTERSECT",VERTEX,{"disambiguationData":[OD(0.0)],"derivedFrom":[subQ1,subQ0]});Q57=makeQuery(id+"F2.imprint","IMPRINT",FACE,{"disambiguationData":[TD([[makeQuery(id+"F2.imprint","IMPRINT",EDGE,{"disambiguationData":[TD([[subQ2,-1.0]])],"derivedFrom":subQ0}),1.0]])]});}
            var Q58;
            {var subQ0=sQuery(id+"F2.wireOp",EDGE,"E14");var subQ1=makeQuery(id+"F1.opRevolve","SWEPT_EDGE",EDGE,{"disambiguationData":[OSD([sQuery(id+"F0.wireOp",EDGE,"E3"),sQuery(id+"F0.wireOp",EDGE,"E4")])]});var subQ2=makeQuery(id+"F2.imprint","INTERSECT",VERTEX,{"disambiguationData":[OD(0.0)],"derivedFrom":[subQ1,subQ0]});Q58=makeQuery(id+"F2.imprint","IMPRINT",FACE,{"disambiguationData":[TD([[makeQuery(id+"F2.imprint","IMPRINT",EDGE,{"disambiguationData":[TD([[subQ2,-1.0]])],"derivedFrom":subQ0}),1.0]])]});}
            var Q59;
            {var subQ0=sQuery(id+"F2.wireOp",EDGE,"E15");var subQ1=makeQuery(id+"F1.opRevolve","SWEPT_EDGE",EDGE,{"disambiguationData":[OSD([sQuery(id+"F0.wireOp",EDGE,"E3"),sQuery(id+"F0.wireOp",EDGE,"E4")])]});var subQ2=makeQuery(id+"F2.imprint","INTERSECT",VERTEX,{"disambiguationData":[OD(0.0)],"derivedFrom":[subQ1,subQ0]});Q59=makeQuery(id+"F2.imprint","IMPRINT",FACE,{"disambiguationData":[TD([[makeQuery(id+"F2.imprint","IMPRINT",EDGE,{"disambiguationData":[TD([[subQ2,-1.0]])],"derivedFrom":subQ0}),1.0]])]});}
            extrude(context, id + "F3", {"entities" : qUnion([Q0, Q1, Q2, Q3, Q4, Q5, Q6, Q7, Q8, Q9, Q10, Q11, Q12, Q13, Q14, Q15, Q16, Q17, Q18, Q19, Q20, Q21, Q22, Q23, Q24, Q25, Q26, Q27, Q28, Q29, Q30, Q31, Q32, Q33, Q34, Q35, Q36, Q37, Q38, Q39, Q40, Q41, Q42, Q43, Q44, Q45, Q46, Q47, Q48, Q49, Q50, Q51, Q52, Q53, Q54, Q55, Q56, Q57, Q58, Q59]), "operationType" : NewBodyOperationType.REMOVE, "oppositeDirection" : true, "depth" : 57.5 * mm});
        }
        {
            var Q0;
            Q0=makeQuery(id+"F3.boolean.opBoolean","COPY",EDGE,{"derivedFrom":makeQuery(id+"F3.opExtrude","CAP_EDGE",EDGE,{"disambiguationData":[OSD([sQuery(id+"F2.wireOp",EDGE,"E14")])],"isStart":false})});
            var Q1;
            Q1=makeQuery(id+"F3.boolean.opBoolean","COPY",EDGE,{"derivedFrom":makeQuery(id+"F3.opExtrude","CAP_EDGE",EDGE,{"disambiguationData":[OSD([sQuery(id+"F2.wireOp",EDGE,"E11")])],"isStart":false})});
            var Q2;
            Q2=makeQuery(id+"F3.boolean.opBoolean","COPY",EDGE,{"derivedFrom":makeQuery(id+"F3.opExtrude","CAP_EDGE",EDGE,{"disambiguationData":[OSD([sQuery(id+"F2.wireOp",EDGE,"E13")])],"isStart":false})});
            var Q3;
            Q3=makeQuery(id+"F3.boolean.opBoolean","COPY",EDGE,{"derivedFrom":makeQuery(id+"F3.opExtrude","CAP_EDGE",EDGE,{"disambiguationData":[OSD([sQuery(id+"F2.wireOp",EDGE,"E12")])],"isStart":false})});
            var Q4;
            Q4=makeQuery(id+"F3.boolean.opBoolean","COPY",EDGE,{"derivedFrom":makeQuery(id+"F3.opExtrude","CAP_EDGE",EDGE,{"disambiguationData":[OSD([sQuery(id+"F2.wireOp",EDGE,"E10")])],"isStart":false})});
            var Q5;
            Q5=makeQuery(id+"F3.boolean.opBoolean","COPY",EDGE,{"derivedFrom":makeQuery(id+"F3.opExtrude","CAP_EDGE",EDGE,{"disambiguationData":[OSD([sQuery(id+"F2.wireOp",EDGE,"E15")])],"isStart":false})});
            fillet(context, id + "F4", {"entities" : qUnion([Q0, Q1, Q2, Q3, Q4, Q5]), "radius" : 5 * mm, "tangentPropagation" : true, "allowEdgeOverflow" : false});
        }
        {
            var Q0;
            Q0=makeQuery(id+"F1.opRevolve","SWEPT_FACE",FACE,{"disambiguationData":[OSD([sQuery(id+"F0.wireOp",EDGE,"E3")])]});
            var sketch = newSketch(context, id + "F5", { "sketchPlane" : qUnion([Q0])});
            skCircle(sketch, "E17", {"center": v(0, 0) * mm, "radius": 11 * mm});
            skSolve(sketch);
        }
        {
            var Q0;
            Q0 = qSketchRegion(id + "F5", true);
            extrude(context, id + "F6", {"entities" : qUnion([Q0]), "operationType" : NewBodyOperationType.REMOVE, "oppositeDirection" : true, "depth" : 8 * mm});
        }
        {
            var Q0;
            Q0=makeQuery(id+"F6.boolean.opBoolean","COPY",FACE,{"derivedFrom":makeQuery(id+"F6.opExtrude","CAP_FACE",FACE,{"disambiguationData":[OSD([sQuery(id+"F5.wireOp",EDGE,"E17")])],"isStart":false})});
            var sketch = newSketch(context, id + "F7", { "sketchPlane" : qUnion([Q0])});
            skCircle(sketch, "E18", {"center": v(0, 0) * mm, "radius": 10.75 * mm});
            skSolve(sketch);
        }
        {
            var Q0;
            Q0 = qSketchRegion(id + "F7", true);
            extrude(context, id + "F8", {"entities" : qUnion([Q0]), "operationType" : NewBodyOperationType.REMOVE, "oppositeDirection" : true, "depth" : 8 * mm});
        }
        {
            var Q0;
            Q0=makeQuery(id+"F8.boolean.opBoolean","COPY",FACE,{"derivedFrom":makeQuery(id+"F8.opExtrude","CAP_FACE",FACE,{"disambiguationData":[OSD([sQuery(id+"F7.wireOp",EDGE,"E18")])],"isStart":false})});
            var sketch = newSketch(context, id + "F9", { "sketchPlane" : qUnion([Q0])});
            skCircle(sketch, "E19", {"center": v(0, 0) * mm, "radius": 7.5 * mm});
            skSolve(sketch);
        }
        {
            var Q0;
            Q0 = qSketchRegion(id + "F9", true);
            extrude(context, id + "F10", {"entities" : qUnion([Q0]), "operationType" : NewBodyOperationType.REMOVE, "oppositeDirection" : true, "depth" : 15 * mm});
        }
        {
            var Q0;
            Q0=makeQuery(id+"F10.boolean.opBoolean","COPY",FACE,{"derivedFrom":makeQuery(id+"F10.opExtrude","CAP_FACE",FACE,{"disambiguationData":[OSD([sQuery(id+"F9.wireOp",EDGE,"E19")])],"isStart":false})});
            var sketch = newSketch(context, id + "F11", { "sketchPlane" : qUnion([Q0])});
            skCircle(sketch, "E20", {"center": v(0, 0) * mm, "radius": 6.2 * mm});
            skSolve(sketch);
        }
        {
            var Q0;
            Q0=makeQuery(id+"F11.imprint","IMPRINT",FACE,{"disambiguationData":[TD([[makeQuery(id+"F11.imprint","IMPRINT",EDGE,{"derivedFrom":sQuery(id+"F11.wireOp",EDGE,"E20")}),-1.0]])]});
            extrude(context, id + "F12", {"entities" : qUnion([Q0]), "operationType" : NewBodyOperationType.ADD, "depth" : 2 * mm});
        }
        {
            var Q0;
            Q0=makeQuery(id+"F12.opExtrude","CAP_EDGE",EDGE,{"disambiguationData":[OSD([sQuery(id+"F11.wireOp",EDGE,"E20")])],"isStart":false});
            fillet(context, id + "F13", {"entities" : qUnion([Q0]), "radius" : 2 * mm, "tangentPropagation" : true, "allowEdgeOverflow" : false});
        }
    });
